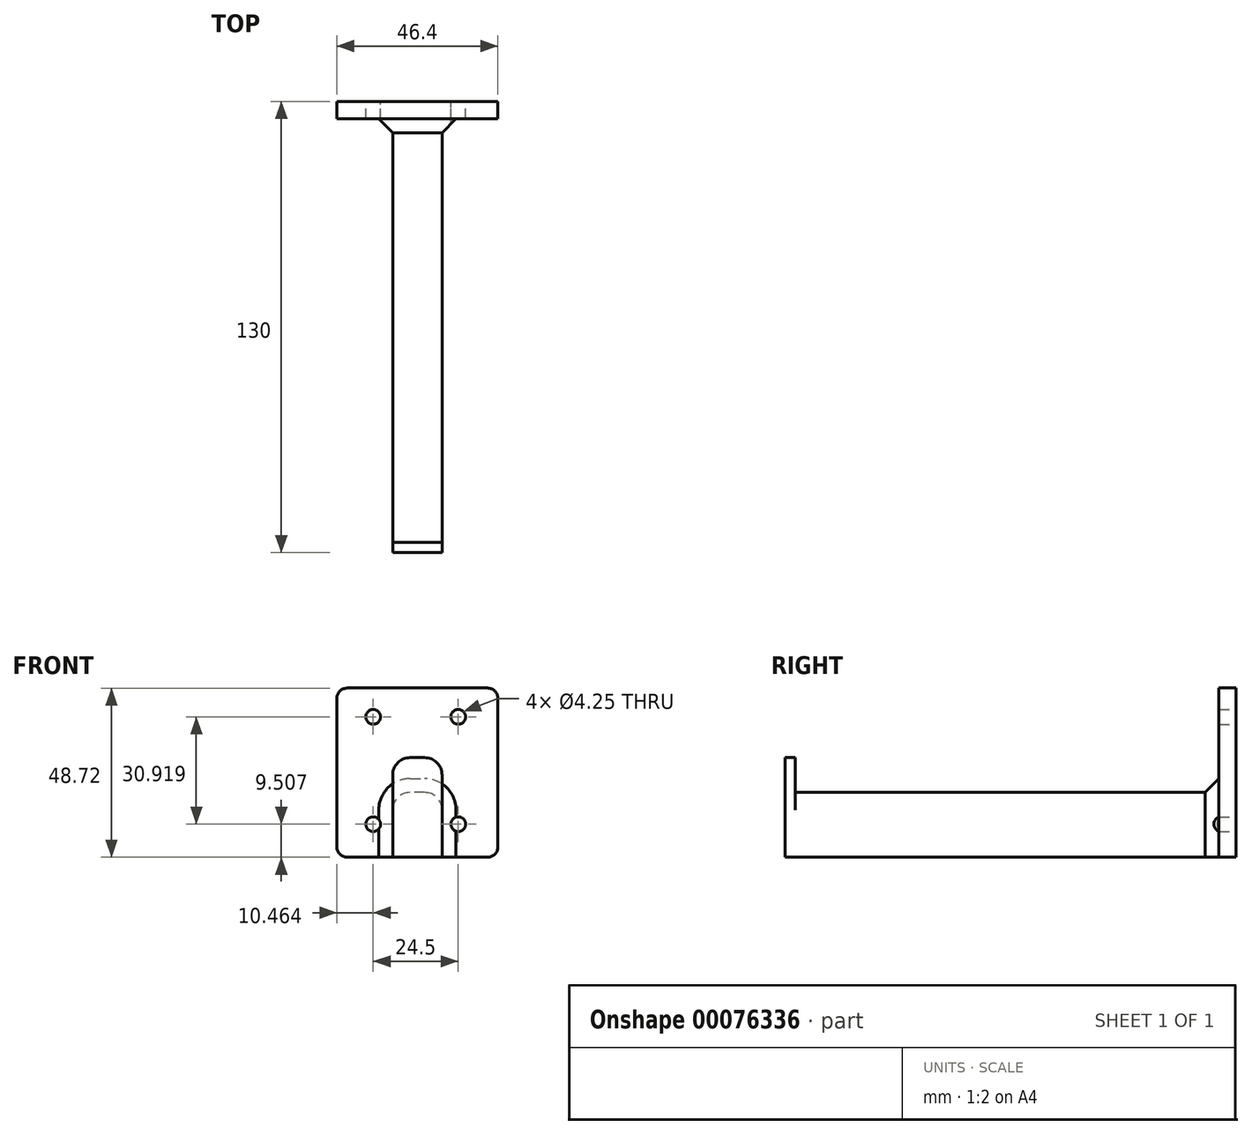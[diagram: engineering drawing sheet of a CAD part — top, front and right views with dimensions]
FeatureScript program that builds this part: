
annotation { "Feature Type Name" : "Feature", "Feature Type Description" : "" }
export const myFeature = defineFeature(function(context is Context, id is Id, definition is map)
    precondition{}
    {
        {
            var Q0;
            Q0=qCreatedBy(makeId("Front.planeOp"),FACE);
            var sketch = newSketch(context, id + "F0", { "sketchPlane" : qUnion([Q0])});
            skLineSegment(sketch, "E0.bottom", {"start": v(-29.81, 31.27) * mm, "end": v(16.6, 31.27) * mm});
            skLineSegment(sketch, "E0.top", {"start": v(-29.81, -17.45) * mm, "end": v(16.6, -17.45) * mm});
            skLineSegment(sketch, "E0.left", {"start": v(-29.81, 31.27) * mm, "end": v(-29.81, -17.45) * mm});
            skLineSegment(sketch, "E0.right", {"start": v(16.6, 31.27) * mm, "end": v(16.6, -17.45) * mm});
            skLineSegment(sketch, "E1.bottom", {"start": v(-13.73, 1.19) * mm, "end": v(0.49, 1.19) * mm});
            skLineSegment(sketch, "E1.top", {"start": v(-13.73, -17.45) * mm, "end": v(0.49, -17.45) * mm});
            skLineSegment(sketch, "E1.left", {"start": v(0.49, 1.19) * mm, "end": v(0.49, -17.45) * mm});
            skLineSegment(sketch, "E1.right", {"start": v(-13.73, 1.19) * mm, "end": v(-13.73, -17.45) * mm});
            skCircle(sketch, "E2", {"center": v(-19.35, 22.98) * mm, "radius": 2.13 * mm});
            skCircle(sketch, "E3.0.1.0", {"center": v(-19.35, -7.94) * mm, "radius": 2.13 * mm});
            skCircle(sketch, "E3.1.0.0", {"center": v(5.15, 22.98) * mm, "radius": 2.13 * mm});
            skCircle(sketch, "E3.1.1.0", {"center": v(5.15, -7.94) * mm, "radius": 2.13 * mm});
            skLineSegment(sketch, "E3.direction1", {"start": v(-19.35, 22.98) * mm, "end": v(5.15, 22.98) * mm, "construction": true});
            skLineSegment(sketch, "E3.direction2", {"start": v(-19.35, 22.98) * mm, "end": v(-19.35, -7.94) * mm, "construction": true});
            skSolve(sketch);
        }
        {
            var Q0;
            Q0=makeQuery(id+"F0.imprint","IMPRINT",FACE,{"disambiguationData":[TD([[makeQuery(id+"F0.imprint","IMPRINT",EDGE,{"derivedFrom":sQuery(id+"F0.wireOp",EDGE,"E0.bottom")}),-1.0]])]});
            extrude(context, id + "F1", {"entities" : qUnion([Q0]), "depth" : 5 * mm});
        }
        {
            var Q0;
            Q0=makeQuery(id+"F0.imprint","IMPRINT",FACE,{"disambiguationData":[TD([[makeQuery(id+"F0.imprint","IMPRINT",EDGE,{"derivedFrom":sQuery(id+"F0.wireOp",EDGE,"E1.bottom")}),-1.0]])]});
            extrude(context, id + "F2", {"entities" : qUnion([Q0]), "operationType" : NewBodyOperationType.ADD, "depth" : 130 * mm});
        }
        {
            var Q0;
            Q0=makeQuery(id+"F2.opExtrude","SWEPT_FACE",FACE,{"disambiguationData":[OSD([sQuery(id+"F0.wireOp",EDGE,"E1.bottom")])]});
            var sketch = newSketch(context, id + "F3", { "sketchPlane" : qUnion([Q0])});
            skLineSegment(sketch, "E4", {"start": v(-13.73, -127) * mm, "end": v(0.49, -127) * mm});
            skSolve(sketch);
        }
        {
            var Q0;
            Q0 = qSketchRegion(id + "F3", true);
            var Q1;
            {var subQ0=sQuery(id+"F3.wireOp",EDGE,"E4");Q1=makeQuery(id+"F3.imprint","IMPRINT",FACE,{"disambiguationData":[TD([[makeQuery(id+"F3.imprint","IMPRINT",EDGE,{"derivedFrom":subQ0}),-1.0]])]});}
            extrude(context, id + "F4", {"entities" : qUnion([Q0, Q1]), "operationType" : NewBodyOperationType.ADD, "depth" : 10.03 * mm});
        }
        {
            var Q0;
            Q0=makeQuery(id+"F2.opExtrude","SWEPT_EDGE",EDGE,{"disambiguationData":[OSD([sQuery(id+"F0.wireOp",EDGE,"E1.bottom"),sQuery(id+"F0.wireOp",EDGE,"E1.left")])]});
            var Q1;
            Q1=makeQuery(id+"F2.opExtrude","SWEPT_EDGE",EDGE,{"disambiguationData":[OSD([sQuery(id+"F0.wireOp",EDGE,"E1.bottom"),sQuery(id+"F0.wireOp",EDGE,"E1.right")])]});
            var Q2;
            Q2=makeQuery(id+"F4.opExtrude","CAP_EDGE",EDGE,{"disambiguationData":[OSD([sQuery(id+"F0.wireOp",EDGE,"E1.bottom"),sQuery(id+"F0.wireOp",EDGE,"E1.right")])],"isStart":false});
            var Q3;
            Q3=makeQuery(id+"F4.opExtrude","CAP_EDGE",EDGE,{"disambiguationData":[OSD([sQuery(id+"F0.wireOp",EDGE,"E1.bottom"),sQuery(id+"F0.wireOp",EDGE,"E1.left")])],"isStart":false});
            fillet(context, id + "F5", {"entities" : qUnion([Q0, Q1, Q2, Q3]), "radius" : 5 * mm, "tangentPropagation" : true, "allowEdgeOverflow" : false});
        }
        {
            var Q0;
            Q0=makeQuery(id+"F1.opExtrude","SWEPT_EDGE",EDGE,{"disambiguationData":[OSD([sQuery(id+"F0.wireOp",EDGE,"E0.bottom"),sQuery(id+"F0.wireOp",EDGE,"E0.left")])]});
            var Q1;
            Q1=makeQuery(id+"F1.opExtrude","SWEPT_EDGE",EDGE,{"disambiguationData":[OSD([sQuery(id+"F0.wireOp",EDGE,"E0.bottom"),sQuery(id+"F0.wireOp",EDGE,"E0.right")])]});
            var Q2;
            Q2=makeQuery(id+"F1.opExtrude","SWEPT_EDGE",EDGE,{"disambiguationData":[OSD([sQuery(id+"F0.wireOp",EDGE,"E0.top"),sQuery(id+"F0.wireOp",EDGE,"E0.left")])]});
            var Q3;
            Q3=makeQuery(id+"F1.opExtrude","SWEPT_EDGE",EDGE,{"disambiguationData":[OSD([sQuery(id+"F0.wireOp",EDGE,"E0.top"),sQuery(id+"F0.wireOp",EDGE,"E0.right")])]});
            fillet(context, id + "F6", {"entities" : qUnion([Q0, Q1, Q2, Q3]), "radius" : 3 * mm, "tangentPropagation" : true, "allowEdgeOverflow" : false});
        }
        {
            var Q0;
            Q0=makeQuery(id+"F1.opExtrude","CAP_EDGE",EDGE,{"disambiguationData":[OSD([sQuery(id+"F0.wireOp",EDGE,"E1.left")])],"isStart":false});
            var Q1;
            {var subQ0=sQuery(id+"F0.wireOp",EDGE,"E1.left");var subQ1=sQuery(id+"F0.wireOp",EDGE,"E1.bottom");Q1=makeQuery(id+"F5.opFillet","BLEND_EDGE",EDGE,{"blendedFrom":[makeQuery(id+"F2.opExtrude","SWEPT_EDGE",EDGE,{"disambiguationData":[OSD([subQ1,subQ0])]}),makeQuery(id+"F1.opExtrude","CAP_FACE",FACE,{"disambiguationData":[OSD([sQuery(id+"F0.wireOp",EDGE,"E0.bottom"),sQuery(id+"F0.wireOp",EDGE,"E0.top"),sQuery(id+"F0.wireOp",EDGE,"E0.left"),sQuery(id+"F0.wireOp",EDGE,"E0.right"),subQ1,subQ0,sQuery(id+"F0.wireOp",EDGE,"E1.right"),sQuery(id+"F0.wireOp",EDGE,"E2"),sQuery(id+"F0.wireOp",EDGE,"E3.0.1.0"),sQuery(id+"F0.wireOp",EDGE,"E3.1.0.0"),sQuery(id+"F0.wireOp",EDGE,"E3.1.1.0")])],"isStart":false})],"blendedInto":[makeQuery(id+"F1.opExtrude","CAP_FACE",FACE,{"disambiguationData":[OSD([sQuery(id+"F0.wireOp",EDGE,"E0.bottom"),sQuery(id+"F0.wireOp",EDGE,"E0.top"),sQuery(id+"F0.wireOp",EDGE,"E0.left"),sQuery(id+"F0.wireOp",EDGE,"E0.right"),subQ1,subQ0,sQuery(id+"F0.wireOp",EDGE,"E1.right"),sQuery(id+"F0.wireOp",EDGE,"E2"),sQuery(id+"F0.wireOp",EDGE,"E3.0.1.0"),sQuery(id+"F0.wireOp",EDGE,"E3.1.0.0"),sQuery(id+"F0.wireOp",EDGE,"E3.1.1.0")])],"isStart":false})]});}
            chamfer(context, id + "F7", {"entities" : qUnion([Q0, Q1]), "width" : 4 * mm, "tangentPropagation" : true});
        }
    });
